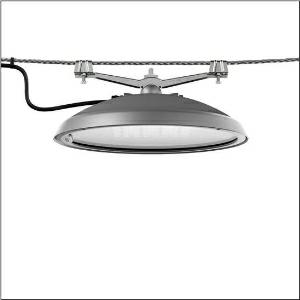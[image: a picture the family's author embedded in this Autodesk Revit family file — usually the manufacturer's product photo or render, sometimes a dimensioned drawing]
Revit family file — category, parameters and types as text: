
# Revit family: dl_r__50_iq_mini___st1_0s_5xa248w31f08ge_208e
name_source: partatom
category: Lighting Fixtures
units: mm (PartAtom-declared; Revit-internal decimal feet)

## family parameters
Cut with Voids When Loaded = No
Host = Face
Light Source = No
Part Type = Normal
Room Calculation Point = No
Round Connector Dimension = Use Diameter
Shared = No

## types (1)
- --- (1 x LED, 5190 lm, 32.7 W, 3000K)
    Apparent Load = 33 VA
    CIE Flux Codes = 37 72 97 100 100
    Color Rendering = 70
    Color Temperature = 3000K
    Default Elevation = 1800 mm
    Description = DL® 50 iQ mini, catenary luminaire, primary light control with lens, of PMMA, primary optical cover: cover, of toughened safety glass, transparent, light distribution: ST1.0s, light emission: direct distribution, primary light characteristic: symmetric, installation type: suspended mounting, LED, High Power LED, rated luminous flux: 5.190lm, luminous efficacy: 159lm/W, light colour: 730, colour temperature: 3000K, control gear: iQ Street-Remote, control: optimised constant luminous flux control (CLO 2.0), Desk-Remote (wireless, voltage-free reading and setting of iQ features in the workshop via application-optimized NFC function/RFID function), Light-Fading, Smart-Wire, Night-Set, Lumen-Switch, Temp-Guard, Auto-Match, Street-Remote, mains connection: 230..240V, AC, 50/60Hz, start of lifetime: 33W, end of service life: 34W, reduction: 16W, luminaire housing, of diecast aluminium, powder-coated, Siteco® metallic grey (DB 702S), diameter: 500mm, height: 115mm, mounting height: 4..12m, protection rating (complete): IP66, insulation class (complete): insulation class II (safety insulation), certification: CE, ENEC, ENEC+, VDE, impact resistance: IK08, permissible operating ambient temperature for outdoor applications: -25..+40°C, standard-compliant lighting for roads and squares, packaging unit: 1 piece

Light Distribution: ST1.0s
    Height = 124 mm  [stored 0.406824 ft]
    Lamp = 1 x LED
    Lamp Light Flux = 5190 lm
    Lamp Power = 32.7 W
    Lamp count = 1
    Length = 500 mm
    Luminous efficacy = 159 lm/W
    Manufacturer = Siteco
    ModVariant = No
    Model = 5XA248W31F08GE
    Number of Poles = 1
    OnlyDefault = Yes
    Power Factor = 1
    Product Name = DL® 50 iQ mini | ST1.0s
    Product group = catenary luminaire
    ProductGroupID = 6300
    Protection Class = Protection class II
    Protection Degree = IP 66
    RLX_Detail_Level = 1
    RLX_Emergency_Light_Flux = 0 lm
    RLX_Emergency_Type = 0
    RLX_Emergency_Type_DB = No
    RlxData = <blob elided: 123393 chars, md5=aa9860c0>
    Socket = socket
    Standby Power = 0 W
    System Light Flux = 5190 lm
    System Power = 33 W
    Type Comments = factory setting: luminous flux: 100 % | dim-lin: 254 | 340 mA
    Type Image = l_1242791.jpg
    URL = http://relux.com
    VarID = @adj_162347
    Voltage = 0 V
    Weight = 0.00 kg
    Width = 0 mm  [stored 0 ft]

note: [stored X ft] marks values corroborated as IEEE doubles in the binary element streams (Revit-internal decimal feet)

## geometry (parser evidence)
native form markers: Blend x4, Sweep x13
no freeform markers — native parametric forms only
